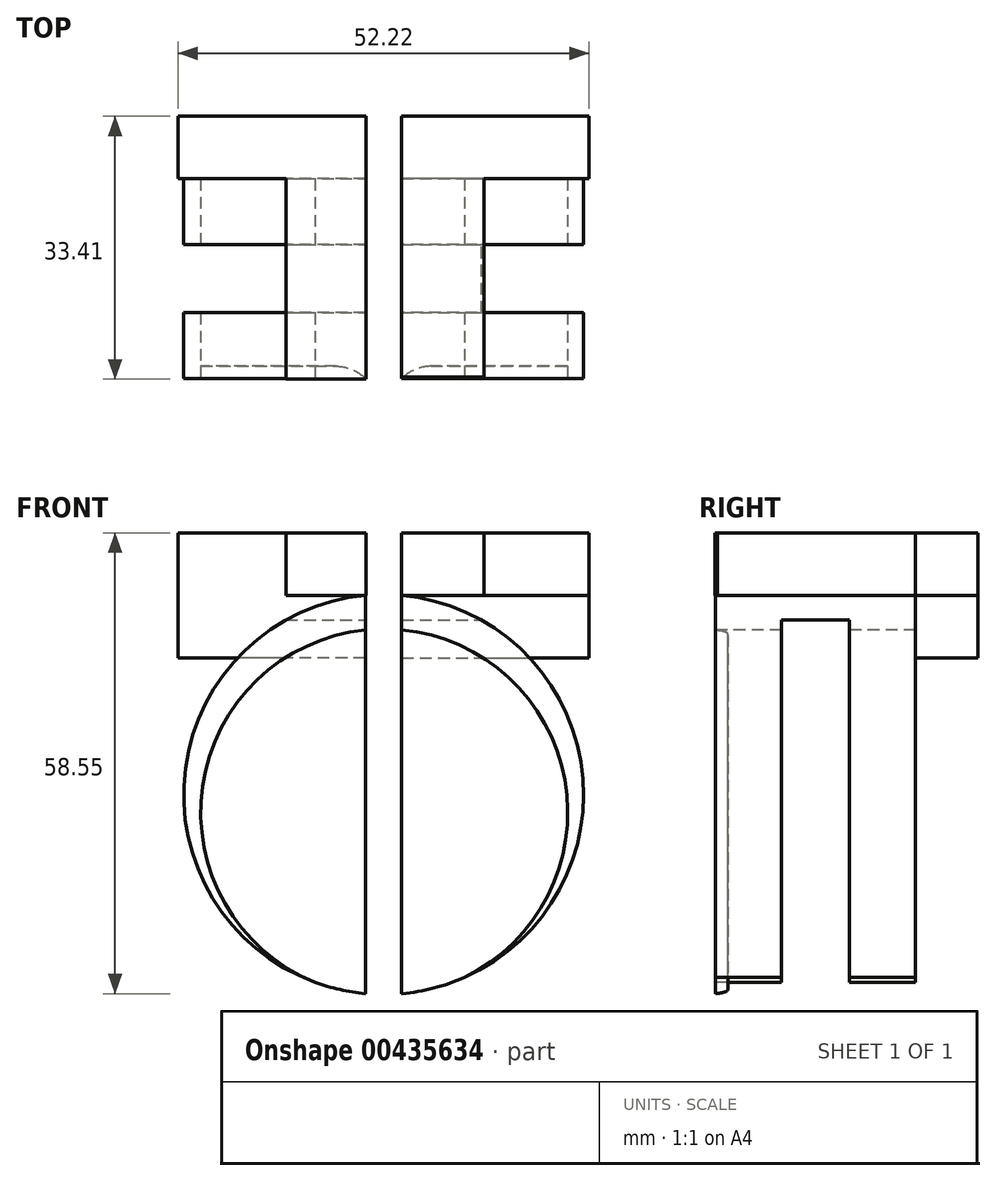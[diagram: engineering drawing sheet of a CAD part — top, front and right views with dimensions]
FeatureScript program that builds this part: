
annotation { "Feature Type Name" : "Feature", "Feature Type Description" : "" }
export const myFeature = defineFeature(function(context is Context, id is Id, definition is map)
    precondition{}
    {
        {
            var Q0;
            Q0=qCreatedBy(makeId("Front.planeOp"),FACE);
            var sketch = newSketch(context, id + "F0", { "sketchPlane" : qUnion([Q0])});
            skCircle(sketch, "E0", {"center": v(0, 0) * mm, "radius": 25.4 * mm});
            skSolve(sketch);
        }
        {
            var Q0;
            Q0=qSketchRegion(id+"F0",true);
            extrude(context, id + "F1", {"entities" : qUnion([Q0]), "endBound" : BoundingType.SYMMETRIC, "depth" : 25.4 * mm});
        }
        {
            var Q0;
            Q0=qCreatedBy(makeId("Right.planeOp"),FACE);
            var sketch = newSketch(context, id + "F2", { "sketchPlane" : qUnion([Q0])});
            skLineSegment(sketch, "E1.bottom", {"start": v(-4.32, 22.16) * mm, "end": v(4.32, 22.16) * mm});
            skLineSegment(sketch, "E1.top", {"start": v(-4.32, -88.93) * mm, "end": v(4.32, -88.93) * mm});
            skLineSegment(sketch, "E1.left", {"start": v(-4.32, 22.16) * mm, "end": v(-4.32, -88.93) * mm});
            skLineSegment(sketch, "E1.right", {"start": v(4.32, 22.16) * mm, "end": v(4.32, -88.93) * mm});
            skPoint(sketch, "E1.middle", {"position": v(0, -33.39) * mm});
            skSolve(sketch);
        }
        {
            var Q0;
            Q0=qSketchRegion(id+"F2",true);
            extrude(context, id + "F3", {"entities" : qUnion([Q0]), "operationType" : NewBodyOperationType.REMOVE, "endBound" : BoundingType.SYMMETRIC, "oppositeDirection" : true, "depth" : 76.2 * mm});
        }
        {
            var Q0;
            Q0=makeQuery(id+"F1.opExtrude","CAP_FACE",FACE,{"disambiguationData":[OSD([sQuery(id+"F0.wireOp",EDGE,"E0")])],"isStart":false});
            var sketch = newSketch(context, id + "F4", { "sketchPlane" : qUnion([Q0])});
            skArc(sketch, "E2", {"start": v(10.28, -23.23) * mm, "mid": v(-0.7, 21.02) * mm, "end": v(-8.73, -23.85) * mm});
            skSolve(sketch);
        }
        {
            var Q0;
            {var subQ0=sQuery(id+"F4.wireOp",EDGE,"E2");Q0=makeQuery(id+"F4.imprint","IMPRINT",FACE,{"disambiguationData":[TD([[makeQuery(id+"F4.imprint","IMPRINT",EDGE,{"derivedFrom":subQ0}),1.0]])]});}
            extrude(context, id + "F5", {"entities" : qUnion([Q0]), "operationType" : NewBodyOperationType.REMOVE, "endBound" : BoundingType.SYMMETRIC, "oppositeDirection" : true, "depth" : 76.2 * mm});
        }
        {
            var Q0;
            Q0=qCreatedBy(makeId("Top.planeOp"),FACE);
            var sketch = newSketch(context, id + "F6", { "sketchPlane" : qUnion([Q0])});
            skLineSegment(sketch, "E3.bottom", {"start": v(2.3, 36.55) * mm, "end": v(-2.3, 36.55) * mm});
            skLineSegment(sketch, "E3.top", {"start": v(2.3, -78) * mm, "end": v(-2.3, -78) * mm});
            skLineSegment(sketch, "E3.left", {"start": v(2.3, 36.55) * mm, "end": v(2.3, -78) * mm});
            skLineSegment(sketch, "E3.right", {"start": v(-2.3, 36.55) * mm, "end": v(-2.3, -78) * mm});
            skPoint(sketch, "E3.middle", {"position": v(0, -20.72) * mm});
            skSolve(sketch);
        }
        {
            var Q0;
            Q0=qSketchRegion(id+"F6",true);
            extrude(context, id + "F7", {"entities" : qUnion([Q0]), "operationType" : NewBodyOperationType.REMOVE, "endBound" : BoundingType.SYMMETRIC, "oppositeDirection" : true, "depth" : 76.2 * mm});
        }
        {
            var Q0;
            {var subQ0=sQuery(id+"F4.wireOp",EDGE,"E2");Q0=makeQuery(id+"F4.imprint","IMPRINT",FACE,{"disambiguationData":[TD([[makeQuery(id+"F4.imprint","IMPRINT",EDGE,{"derivedFrom":subQ0}),1.0]])]});}
            extrude(context, id + "F8", {"entities" : qUnion([Q0]), "oppositeDirection" : true, "depth" : 1.59 * mm});
        }
        {
            var Q0;
            Q0=makeQuery(id+"F6.imprint","IMPRINT",FACE,{"disambiguationData":[TD([[makeQuery(id+"F6.imprint","IMPRINT",EDGE,{"derivedFrom":sQuery(id+"F6.wireOp",EDGE,"E3.bottom")}),1.0]])]});
            extrude(context, id + "F9", {"entities" : qUnion([Q0]), "operationType" : NewBodyOperationType.REMOVE, "oppositeDirection" : true, "depth" : 76.2 * mm});
        }
        {
            var Q0;
            Q0=makeQuery(id+"F6.imprint","IMPRINT",FACE,{"disambiguationData":[TD([[makeQuery(id+"F6.imprint","IMPRINT",EDGE,{"derivedFrom":sQuery(id+"F6.wireOp",EDGE,"E3.bottom")}),1.0]])]});
            extrude(context, id + "F10", {"entities" : qUnion([Q0]), "operationType" : NewBodyOperationType.REMOVE, "endBound" : BoundingType.SYMMETRIC, "oppositeDirection" : true, "depth" : 50.8 * mm});
        }
        {
            var Q0;
            Q0=makeQuery(id+"F10.boolean.opBoolean","INTERSECT",EDGE,{"derivedFrom":[makeQuery(id+"F8.opExtrude","CAP_FACE",FACE,{"disambiguationData":[OSD([sQuery(id+"F0.wireOp",EDGE,"E0"),sQuery(id+"F4.wireOp",EDGE,"E2")])],"isStart":false}),makeQuery(id+"F10.opExtrude","SWEPT_FACE",FACE,{"disambiguationData":[OSD([sQuery(id+"F6.wireOp",EDGE,"E3.left")])]})]});
            var Q1;
            Q1=makeQuery(id+"F10.boolean.opBoolean","INTERSECT",EDGE,{"derivedFrom":[makeQuery(id+"F8.opExtrude","CAP_FACE",FACE,{"disambiguationData":[OSD([sQuery(id+"F0.wireOp",EDGE,"E0"),sQuery(id+"F4.wireOp",EDGE,"E2")])],"isStart":false}),makeQuery(id+"F10.opExtrude","SWEPT_FACE",FACE,{"disambiguationData":[OSD([sQuery(id+"F6.wireOp",EDGE,"E3.right")])]})]});
            fillet(context, id + "F11", {"entities" : qUnion([Q0, Q1]), "radius" : 5.08 * mm, "tangentPropagation" : true, "allowEdgeOverflow" : false});
        }
        {
            var Q0;
            {var subQ0=sQuery(id+"F0.wireOp",EDGE,"E0");var subQ2=makeQuery(id+"F1.opExtrude","CAP_FACE",FACE,{"disambiguationData":[OSD([subQ0])],"isStart":true});Q0=makeQuery(id+"F7.boolean.opBoolean","SPLIT",FACE,{"disambiguationData":[TD([makeQuery(id+"F7.opExtrude","SWEPT_FACE",FACE,{"disambiguationData":[OSD([sQuery(id+"F6.wireOp",EDGE,"E3.left")])]})])],"derivedFrom":subQ2});}
            var sketch = newSketch(context, id + "F12", { "sketchPlane" : qUnion([Q0])});
            skLineSegment(sketch, "E4.bottom", {"start": v(-2.3, 25.3) * mm, "end": v(-2.3, 25.3) * mm});
            skLineSegment(sketch, "E4.top", {"start": v(-2.3, 17.36) * mm, "end": v(-2.3, 17.36) * mm});
            skLineSegment(sketch, "E4.left", {"start": v(-2.3, 25.3) * mm, "end": v(-2.3, 17.36) * mm});
            skLineSegment(sketch, "E4.right", {"start": v(-2.3, 25.3) * mm, "end": v(-2.3, 17.36) * mm});
            skLineSegment(sketch, "E5.bottom", {"start": v(-2.3, 17.36) * mm, "end": v(-26.11, 17.36) * mm});
            skLineSegment(sketch, "E5.top", {"start": v(-2.3, 25.3) * mm, "end": v(-26.11, 25.3) * mm});
            skLineSegment(sketch, "E5.left", {"start": v(-2.3, 17.36) * mm, "end": v(-2.3, 25.3) * mm});
            skLineSegment(sketch, "E5.right", {"start": v(-26.11, 17.36) * mm, "end": v(-26.11, 25.3) * mm});
            skSolve(sketch);
        }
        {
            var Q0;
            Q0=qSketchRegion(id+"F12",true);
            extrude(context, id + "F13", {"entities" : qUnion([Q0]), "operationType" : NewBodyOperationType.ADD, "depth" : 7.94 * mm});
        }
        {
            var Q0;
            {var subQ0=sQuery(id+"F0.wireOp",EDGE,"E0");var subQ2=makeQuery(id+"F1.opExtrude","CAP_FACE",FACE,{"disambiguationData":[OSD([subQ0])],"isStart":true});Q0=makeQuery(id+"F7.boolean.opBoolean","SPLIT",FACE,{"disambiguationData":[TD([makeQuery(id+"F7.opExtrude","SWEPT_FACE",FACE,{"disambiguationData":[OSD([sQuery(id+"F6.wireOp",EDGE,"E3.right")])]})])],"derivedFrom":subQ2});}
            var sketch = newSketch(context, id + "F14", { "sketchPlane" : qUnion([Q0])});
            skPoint(sketch, "E6.oppositeSnap0", {"position": v(2.3, 23.1) * mm});
            skLineSegment(sketch, "E6.bottom", {"start": v(2.3, 25.3) * mm, "end": v(2.3, 25.3) * mm});
            skLineSegment(sketch, "E6.top", {"start": v(2.3, 17.36) * mm, "end": v(2.3, 17.36) * mm});
            skLineSegment(sketch, "E6.left", {"start": v(2.3, 25.3) * mm, "end": v(2.3, 17.36) * mm});
            skLineSegment(sketch, "E6.right", {"start": v(2.3, 25.3) * mm, "end": v(2.3, 17.36) * mm});
            skLineSegment(sketch, "E7.bottom", {"start": v(2.3, 25.3) * mm, "end": v(26.11, 25.3) * mm});
            skLineSegment(sketch, "E7.top", {"start": v(2.3, 17.36) * mm, "end": v(26.11, 17.36) * mm});
            skLineSegment(sketch, "E7.right", {"start": v(26.11, 25.3) * mm, "end": v(26.11, 17.36) * mm});
            skLineSegment(sketch, "E8.bottom", {"start": v(26.11, 25.3) * mm, "end": v(2.25, 25.3) * mm});
            skLineSegment(sketch, "E8.top", {"start": v(26.11, 33.25) * mm, "end": v(2.25, 33.25) * mm});
            skLineSegment(sketch, "E8.left", {"start": v(26.11, 25.3) * mm, "end": v(26.11, 33.25) * mm});
            skLineSegment(sketch, "E8.right", {"start": v(2.25, 25.3) * mm, "end": v(2.25, 33.25) * mm});
            skSolve(sketch);
        }
        {
            var Q0;
            Q0=qSketchRegion(id+"F14",true);
            extrude(context, id + "F15", {"entities" : qUnion([Q0]), "operationType" : NewBodyOperationType.ADD, "depth" : 7.94 * mm});
        }
        {
            var Q0;
            Q0=makeQuery(id+"F15.opExtrude","SWEPT_FACE",FACE,{"disambiguationData":[OSD([sQuery(id+"F14.wireOp",EDGE,"E8.top")])]});
            var sketch = newSketch(context, id + "F16", { "sketchPlane" : qUnion([Q0])});
            skLineSegment(sketch, "E9.bottom", {"start": v(-2.25, 12.7) * mm, "end": v(-12.42, 12.7) * mm});
            skLineSegment(sketch, "E9.top", {"start": v(-2.25, -12.77) * mm, "end": v(-12.42, -12.77) * mm});
            skLineSegment(sketch, "E9.left", {"start": v(-2.25, 12.7) * mm, "end": v(-2.25, -12.77) * mm});
            skLineSegment(sketch, "E9.right", {"start": v(-12.42, 12.7) * mm, "end": v(-12.42, -12.77) * mm});
            skSolve(sketch);
        }
        {
            var Q0;
            Q0=qSketchRegion(id+"F16",true);
            extrude(context, id + "F17", {"entities" : qUnion([Q0]), "operationType" : NewBodyOperationType.ADD, "oppositeDirection" : true, "depth" : 7.94 * mm});
        }
        {
            var Q0;
            Q0=makeQuery(id+"F17.boolean.opBoolean","MERGE",FACE,{"derivedFrom":[makeQuery(id+"F15.opExtrude","SWEPT_FACE",FACE,{"disambiguationData":[OSD([sQuery(id+"F14.wireOp",EDGE,"E8.top")])]}),makeQuery(id+"F17.opExtrude","CAP_FACE",FACE,{"disambiguationData":[OSD([sQuery(id+"F16.wireOp",EDGE,"E9.bottom"),sQuery(id+"F16.wireOp",EDGE,"E9.top"),sQuery(id+"F16.wireOp",EDGE,"E9.left"),sQuery(id+"F16.wireOp",EDGE,"E9.right")])],"isStart":true})]});
            var sketch = newSketch(context, id + "F18", { "sketchPlane" : qUnion([Q0])});
            skLineSegment(sketch, "E10", {"start": v(-12.42, -12.77) * mm, "end": v(-7.33, -12.77) * mm});
            skLineSegment(sketch, "E11", {"start": v(-7.33, -12.77) * mm, "end": v(-7.33, -5.77) * mm});
            skLineSegment(sketch, "E12", {"start": v(-7.33, -5.77) * mm, "end": v(-7.33, 2.2) * mm});
            skLineSegment(sketch, "E13", {"start": v(-7.33, 2.2) * mm, "end": v(-7.33, 10.17) * mm});
            skLineSegment(sketch, "E14", {"start": v(-7.33, 10.17) * mm, "end": v(-7.33, 18.14) * mm});
            skPoint(sketch, "E15", {"position": v(-7.33, -5.77) * mm});
            skPoint(sketch, "E16", {"position": v(-7.33, 2.2) * mm});
            skPoint(sketch, "E17", {"position": v(-7.33, 10.17) * mm});
            skPoint(sketch, "E18", {"position": v(-7.33, 18.14) * mm});
            skSolve(sketch);
        }
        {
            var Q0;
            {var subQ3=sQuery(id+"F18.wireOp",EDGE,"E10");Q0=makeQuery(id+"F18.imprint","IMPRINT",FACE,{"disambiguationData":[TD([[makeQuery(id+"F18.imprint","IMPRINT",EDGE,{"derivedFrom":subQ3}),-1.0]])]});}
            var sketch = newSketch(context, id + "F19", { "sketchPlane" : qUnion([Q0])});
            skSolve(sketch);
        }
        {
            var Q0;
            Q0=makeQuery(id+"F13.opExtrude","SWEPT_FACE",FACE,{"disambiguationData":[OSD([sQuery(id+"F12.wireOp",EDGE,"E5.top")])]});
            var sketch = newSketch(context, id + "F20", { "sketchPlane" : qUnion([Q0])});
            skLineSegment(sketch, "E19", {"start": v(2.3, 20.64) * mm, "end": v(26.11, 20.64) * mm});
            skPoint(sketch, "E20.endSnap0", {"position": v(2.3, 16.67) * mm});
            skLineSegment(sketch, "E21", {"start": v(2.3, 20.64) * mm, "end": v(2.3, -12.46) * mm});
            skLineSegment(sketch, "E22", {"start": v(2.3, -12.46) * mm, "end": v(12.75, -12.46) * mm});
            skLineSegment(sketch, "E23", {"start": v(12.75, -12.46) * mm, "end": v(12.75, 12.7) * mm});
            skSolve(sketch);
        }
        {
            var Q0;
            {var subQ5=sQuery(id+"F20.wireOp",EDGE,"E19");Q0=makeQuery(id+"F20.imprint","IMPRINT",FACE,{"disambiguationData":[TD([[makeQuery(id+"F20.imprint","IMPRINT",EDGE,{"derivedFrom":subQ5}),-1.0]])]});}
            var Q1;
            {var subQ3=sQuery(id+"F20.wireOp",EDGE,"E22");Q1=makeQuery(id+"F20.imprint","IMPRINT",FACE,{"disambiguationData":[TD([[makeQuery(id+"F20.imprint","IMPRINT",EDGE,{"derivedFrom":subQ3}),1.0]])]});}
            extrude(context, id + "F21", {"entities" : qUnion([Q0, Q1]), "depth" : 7.94 * mm});
        }
    });
